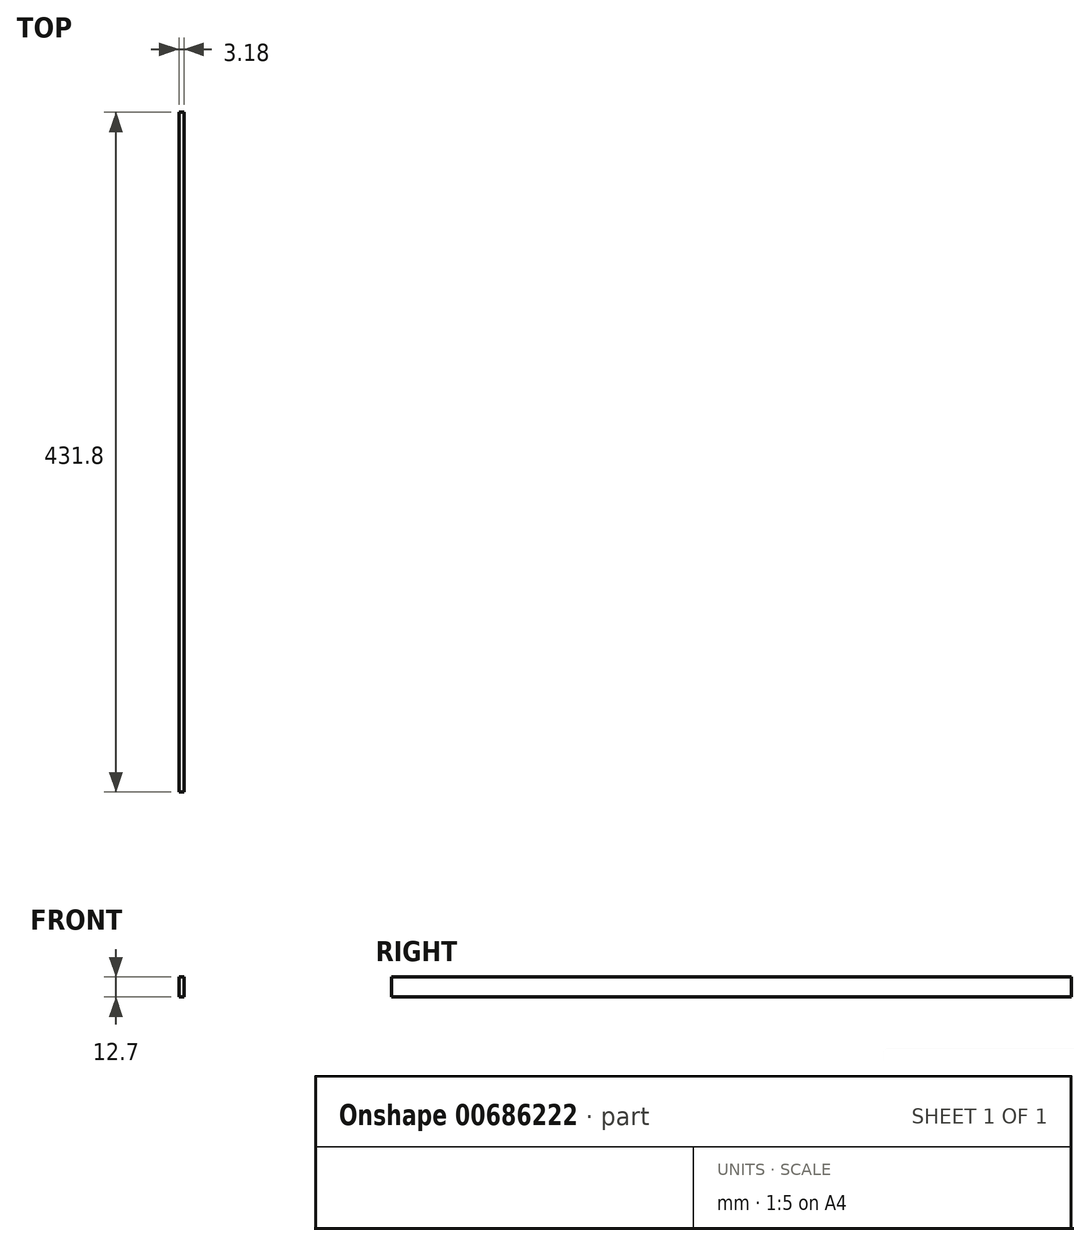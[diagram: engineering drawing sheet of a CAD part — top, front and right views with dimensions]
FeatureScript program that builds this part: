
annotation { "Feature Type Name" : "Feature", "Feature Type Description" : "" }
export const myFeature = defineFeature(function(context is Context, id is Id, definition is map)
    precondition{}
    {
        {
            var Q0;
            Q0=qCreatedBy(makeId("Front.planeOp"),FACE);
            var sketch = newSketch(context, id + "F0", { "sketchPlane" : qUnion([Q0])});
            skLineSegment(sketch, "E0.bottom", {"start": v(-1.59, 6.35) * mm, "end": v(1.59, 6.35) * mm});
            skLineSegment(sketch, "E0.top", {"start": v(-1.59, -6.35) * mm, "end": v(1.59, -6.35) * mm});
            skLineSegment(sketch, "E0.left", {"start": v(-1.59, 6.35) * mm, "end": v(-1.59, -6.35) * mm});
            skLineSegment(sketch, "E0.right", {"start": v(1.59, 6.35) * mm, "end": v(1.59, -6.35) * mm});
            skPoint(sketch, "E0.middle", {"position": v(0, 0) * mm});
            skSolve(sketch);
        }
        {
            var Q0;
            Q0 = qSketchRegion(id + "F0", true);
            extrude(context, id + "F1", {"entities" : qUnion([Q0]), "endBound" : BoundingType.SYMMETRIC, "depth" : 431.8 * mm, "offsetDistance" : 25.4 * mm});
        }
    });
